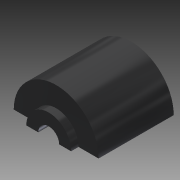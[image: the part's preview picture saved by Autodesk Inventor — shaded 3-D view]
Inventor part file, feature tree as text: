
AUTODESK INVENTOR PART (.ipt)
format: ipt  version: 2013 (Build 170138000, 138)  size: 137,216 bytes
history: native  units: in
note: dims shown in document units (in); Inventor stores cm internally (conversion verified against a paired STEP export)
features: sketch x2, chamfer x1, other x1, split x1, extrude x1, revolve x1, imported_body x1, projected_geometry x1
ambient origin geometry x8: Origin, YZ Plane, XZ Plane, XY Plane, X Axis, Y Axis, Z Axis, Center Point
feature tree (9):
  chamfer  "Chamfer2"  Distance=0.0625in
  other  "217-2428-011 Rev2 1"
  split  "Split1"
  extrude  "Extrusion1"  Depth=0.25in
  revolve  "Revolution1"  [1 undecoded]
  imported_body  "Base1"
  sketch  "Sketch1"  dims[d0=0.375in d1=0.0625in d2=0.0in]
  sketch  "Sketch2"  dims[d3=0.125in d5=0.25in d6=0.1875in d7=90.0deg]
  projected_geometry  "Project Cut Edges1"
note: 1 required parameter value undecoded (feature->parameter linkage not recoverable at this tier; creation-order binding heuristic only, values carry confidence <= 0.55)
